# Revit family: РИДАН_Термостатические элементы серии TR 9000 Ultra
name_source: partatom
category: Арматура трубопроводов
units: mm (PartAtom-declared; Revit-internal decimal feet)

## family parameters
Всегда вертикально = Да
На основе рабочей плоскости = Нет
Общий = Да
При загрузке вырезать с полостями = Нет
Размер круглого соединителя = Использовать диаметр
Тип детали = Нормальный

## types (4) — shared parameters
ADSK_Версия Revit = 2019
ADSK_Версия семейства = 1.0
ADSK_Единица измерения = шт.
ADSK_Завод-изготовитель = ООО «Ридан-Трейд»
ADSK_Количество = 1
ADSK_Материал = <По категории>
LT = TR9000
zero-valued in all types: ADSK_Масса

## per-type parameters (varying)
| type | ADSK_Код изделия | ADSK_Наименование | RA | Артикул | Гайка |
| TR 9000 Ultra | 013G9000R | Термостатический элемент со встроен ным датчиком, присоединение RTR/RA | Да | 013G9000R | Нет |
| TR 9001 Ultra | 013G9001R | Термостатический элемент со встроен ным датчиком, присоединение М30х1,5 | Нет | 013G9001R | Да |
| TR 9005 Ultra | 013G9005R | Термостатический элемент с выносным  датчиком, присоединение RTR/RA.  Длина капиллярной трубки 2 м | Да | 013G9005R | Нет |
| TR 9006 Ultra | 013G9006R | Термостатический элемент с выносным  датчиком, присоединение М30х1,5.  Длина капиллярной трубки 2 м | Нет | 013G9006R | Да |

note: column(s) folded — value = type name in every type: ADSK_Марка
